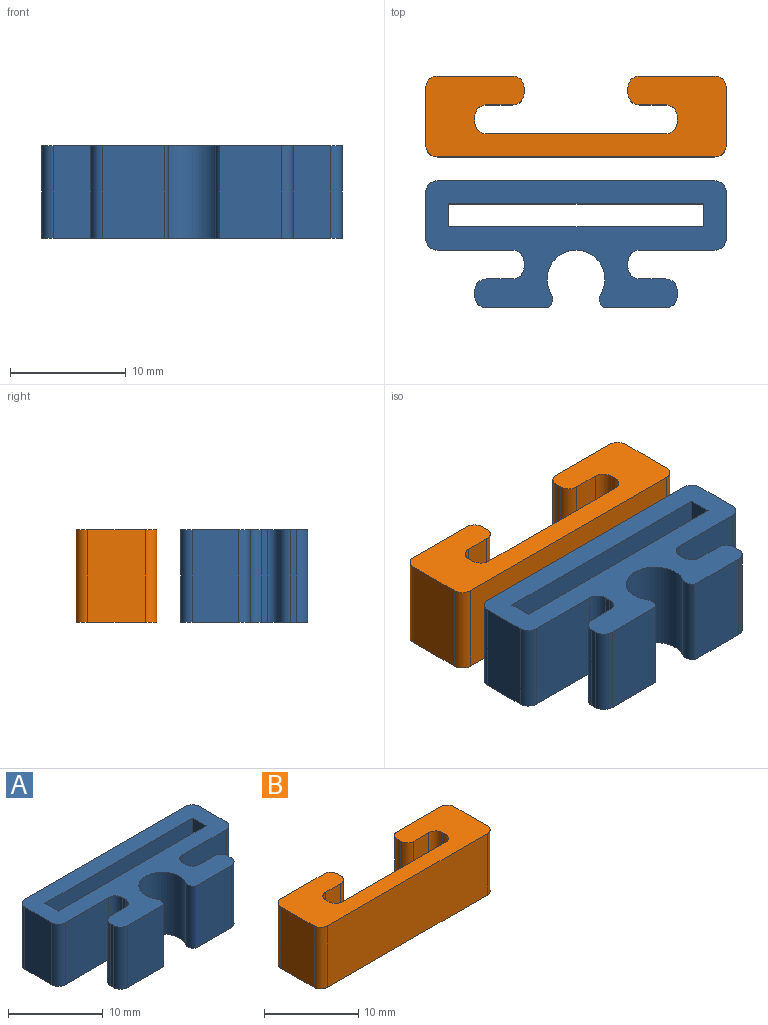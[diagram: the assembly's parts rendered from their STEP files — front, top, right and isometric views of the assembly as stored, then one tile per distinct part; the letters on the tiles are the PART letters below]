
ASSEMBLY  parts=2 mates=3
PART A: 34 faces, bbox 26x11x8 mm
  f0: cylinder r=1mm len=8mm, axis (0,0,-1), area 11mm2, adj f1,f31,f32,f33
  f1: plane 8x5.38mm, normal (0,-1,0), area 43mm2, adj f0,f2,f32,f33
  f2: cylinder r=1mm len=8mm, axis (0,0,-1), area 12.6mm2, adj f1,f3,f32,f33
  f3: plane 8x0.5mm, normal (1,0,0), area 4mm2, adj f2,f4,f32,f33
  f4: cylinder r=1mm len=8mm, axis (0,0,-1), area 12.6mm2, adj f3,f5,f32,f33
  f5: plane 8x2.25mm, normal (0,1,0), area 18mm2, adj f4,f6,f32,f33
  f6: cylinder r=1mm len=8mm, axis (0,0,-1), area 12.6mm2, adj f5,f7,f32,f33
  f7: plane 8x0.5mm, normal (1,0,0), area 4mm2, adj f6,f8,f32,f33
  f8: cylinder r=1mm len=8mm, axis (0,0,-1), area 12.6mm2, adj f7,f9,f32,f33
  f9: plane 8x6.5mm, normal (0,-1,0), area 52mm2, adj f8,f10,f32,f33
  f10: cylinder r=1mm len=8mm, axis (0,0,-1), area 12.6mm2, adj f9,f11,f32,f33
  f11: plane 8x4mm, normal (1,0,0), area 32mm2, adj f10,f12,f32,f33
  f12: cylinder r=1mm len=8mm, axis (0,0,-1), area 12.6mm2, adj f11,f13,f32,f33
  f13: plane 24x8mm, normal (0,1,0), area 192mm2, adj f12,f14,f32,f33
  f14: cylinder r=1mm len=8mm, axis (0,0,-1), area 12.6mm2, adj f13,f15,f32,f33
  f15: plane 8x4mm, normal (-1,0,0), area 32mm2, adj f14,f16,f32,f33
  f16: cylinder r=1mm len=8mm, axis (0,0,-1), area 12.6mm2, adj f15,f17,f32,f33
  f17: plane 8x6.5mm, normal (0,-1,0), area 52mm2, adj f16,f18,f32,f33
  f18: cylinder r=1mm len=8mm, axis (0,0,-1), area 12.6mm2, adj f17,f19,f32,f33
  f19: plane 8x0.5mm, normal (-1,0,0), area 4mm2, adj f18,f20,f32,f33
  f20: cylinder r=1mm len=8mm, axis (0,0,-1), area 12.6mm2, adj f19,f21,f32,f33
  f21: plane 8x2.25mm, normal (0,1,0), area 18mm2, adj f20,f22,f32,f33
  f22: cylinder r=1mm len=8mm, axis (0,0,-1), area 12.6mm2, adj f21,f23,f32,f33
  f23: plane 8x0.5mm, normal (-1,0,0), area 4mm2, adj f22,f24,f32,f33
  f24: cylinder r=1mm len=8mm, axis (0,0,-1), area 12.6mm2, adj f23,f25,f32,f33
  f25: plane 8x5.38mm, normal (0,-1,0), area 43mm2, adj f24,f26,f32,f33
  f26: cylinder r=1mm len=8mm, axis (0,0,-1), area 11mm2, adj f25,f31,f32,f33
  f27: plane 22x8mm, normal (0,1,0), area 176mm2, adj f28,f30,f32,f33
  f28: plane 8x2mm, normal (1,0,0), area 16mm2, adj f27,f29,f32,f33
  f29: plane 22x8mm, normal (0,-1,0), area 176mm2, adj f28,f30,f32,f33
  f30: plane 8x2mm, normal (-1,0,0), area 16mm2, adj f27,f29,f32,f33
  f31: cylinder r=2.5mm len=8mm, axis (0,0,-1), area 83.8mm2, adj f0,f26,f32,f33
  f32: plane 26x11mm, normal (0,0,1), area 156.3mm2, adj f0,f1,f2,f3,f4,f5,f6,f7
  f33: plane 26x11mm, normal (0,0,-1), area 156.3mm2, adj f0,f1,f2,f3,f4,f5,f6,f7
PART B: 26 faces, bbox 26x7x8 mm
  f0: cylinder r=1mm len=8mm, axis (0,0,-1), area 12.6mm2, adj f1,f23,f24,f25
  f1: plane 8x2.25mm, normal (0,-1,0), area 18mm2, adj f0,f2,f24,f25
  f2: cylinder r=1mm len=8mm, axis (0,0,-1), area 12.6mm2, adj f1,f3,f24,f25
  f3: plane 8x0.5mm, normal (1,0,0), area 4mm2, adj f2,f4,f24,f25
  f4: cylinder r=1mm len=8mm, axis (0,0,-1), area 12.6mm2, adj f3,f5,f24,f25
  f5: plane 8x6.5mm, normal (0,1,0), area 52mm2, adj f4,f6,f24,f25
  f6: cylinder r=1mm len=8mm, axis (0,0,-1), area 12.6mm2, adj f5,f7,f24,f25
  f7: plane 8x5mm, normal (-1,0,0), area 40mm2, adj f6,f8,f24,f25
  f8: cylinder r=1mm len=8mm, axis (0,0,-1), area 12.6mm2, adj f7,f9,f24,f25
  f9: plane 24x8mm, normal (0,-1,0), area 192mm2, adj f8,f10,f24,f25
  f10: cylinder r=1mm len=8mm, axis (0,0,-1), area 12.6mm2, adj f9,f11,f24,f25
  f11: plane 8x5mm, normal (1,0,0), area 40mm2, adj f10,f12,f24,f25
  f12: cylinder r=1mm len=8mm, axis (0,0,-1), area 12.6mm2, adj f11,f13,f24,f25
  f13: plane 8x6.5mm, normal (0,1,0), area 52mm2, adj f12,f14,f24,f25
  f14: cylinder r=1mm len=8mm, axis (0,0,-1), area 12.6mm2, adj f13,f15,f24,f25
  f15: plane 8x0.5mm, normal (-1,0,0), area 4mm2, adj f14,f16,f24,f25
  f16: cylinder r=1mm len=8mm, axis (0,0,-1), area 12.6mm2, adj f15,f17,f24,f25
  f17: plane 8x2.25mm, normal (0,-1,0), area 18mm2, adj f16,f18,f24,f25
  f18: cylinder r=1mm len=8mm, axis (0,0,-1), area 12.6mm2, adj f17,f19,f24,f25
  f19: plane 8x0.5mm, normal (-1,0,0), area 4mm2, adj f18,f20,f24,f25
  f20: cylinder r=1mm len=8mm, axis (0,0,-1), area 12.6mm2, adj f19,f21,f24,f25
  f21: plane 15.5x8mm, normal (0,1,0), area 124mm2, adj f20,f22,f24,f25
  f22: cylinder r=1mm len=8mm, axis (0,0,-1), area 12.6mm2, adj f21,f23,f24,f25
  f23: plane 8x0.5mm, normal (1,0,0), area 4mm2, adj f0,f22,f24,f25
  f24: plane 26x7mm, normal (0,0,1), area 114.9mm2, adj f0,f1,f2,f3,f4,f5,f6,f7
  f25: plane 26x7mm, normal (0,0,-1), area 114.9mm2, adj f0,f1,f2,f3,f4,f5,f6,f7
PLACE A at identity fixed
PLACE B t=(0,15.06,0)mm
MATE planar A.f15 <-> B.f7  axis (-1,0,0) through (-13,0,4)mm
MATE parallel A.f13 <-> B.f9  axis (0,1,0) through (0,3,4)mm
MATE planar A.f33 <-> B.f25  axis (0,0,1) through (-5.5,-3,0)mm
